# Revit family: Genie_Site_ArticulatingBoom_(SX-150)A
name_source: partatom
category: Site
revit_build: Autodesk Revit 2018 (Build: 20190510_1515(x64)
units: mm (PartAtom-declared; Revit-internal decimal feet)

## family parameters
Always vertical = Yes
Cut with Voids When Loaded = No
OmniClass Number = 23.50.85.17.11
OmniClass Title = Electric and Battery Telescoping Platforms
Part Type = Normal
Round Connector Dimension = Use Diameter
Shared = No
Work Plane-Based = No

## types (1)
- SX-150
    Assembly Code = E1030900
    AssetType = Fixed
    BIMObjectName = Genie_Site_ArticulatingBoom_(SX-150)
    ClassificationName = Uniclass2015
    ClassificationValue = Pr_65_80_47_95
    Color = Grey & Blue
    Cost = 0 $
    Description = The Genie® SX™-150 telescopic boom lift offers uncompromising productivity and industry-leading capacity through the full working envelope. This Genie boom is designed to perform in even the most extreme construction, maintenance, telecommunications, gas and oil, chemical maintenance, and large utility applications.
    DocumentationLiterature = https://www.genielift.com
    DocumentationTechnical = https://www.genielift.com
    DurationUnit = Years
    ExpectedLife = 0
    Features = Genie XChassis™ system extends and retracts to provide stability on the job and a narrow profile for transport. 3.05 m (10 ft) rotating jib with 135˚ vertical and 60˚ horizontal articulation to easily position workers and gear. Standard 2.44 m (8 ft) self-levelling platform with an unrestricted capacity of 340 kg (750 lb). Drive-enable at full height for more productivity on the jobsite. Features a working envelope ideal for the most extreme access jobs with a working height of 48.33 m (158 ft) and a horizontal reach of 24.38 m (80 ft).
    Finish = Painted Steel
    IfcExportAs = IfcTransportElement
    IfcExportType = IfcTransportElementType
    Keynote = X
    Manufacturer = Genie
    ManufacturerName = Genie
    Material = Painted Steel
    Model = Genie - Articulating Boom
    ModelNumber = SX-150
    ModelReference = Genie - Articulating Boom
    NBSDescription = Vertical lifting platforms
    NBSObjectName = Genie - Vertical lifting platforms
    NBSReference = 90-80-65/350
    NominalDepth = 2490 mm
    NominalHeight = 3050 mm
    NominalLength = 16180 mm
    ProductionYear = 2019
    Size = 2.49m x 3.05m x 16.18m
    Type Comments = SX-150
    TypeName = Genie - Articulating Boom
    URL = http://www.genielift.co.uk
    WarrantyDurationLabor = 0
    WarrantyDurationParts = 0
    WarrantyDurationUnit = Years
    WarrantyGuarantorLabor = http://www.genielift.co.uk
    WarrantyGuarantorParts = http://www.genielift.co.uk
    _BSBibleVersion = 15
    _BimSpecGuid = 0
    _CurrentRevision = 1
    _DistributedBy = www.bimstore.co.uk

## geometry (parser evidence)
native form markers: Sweep x32
no freeform markers — native parametric forms only
